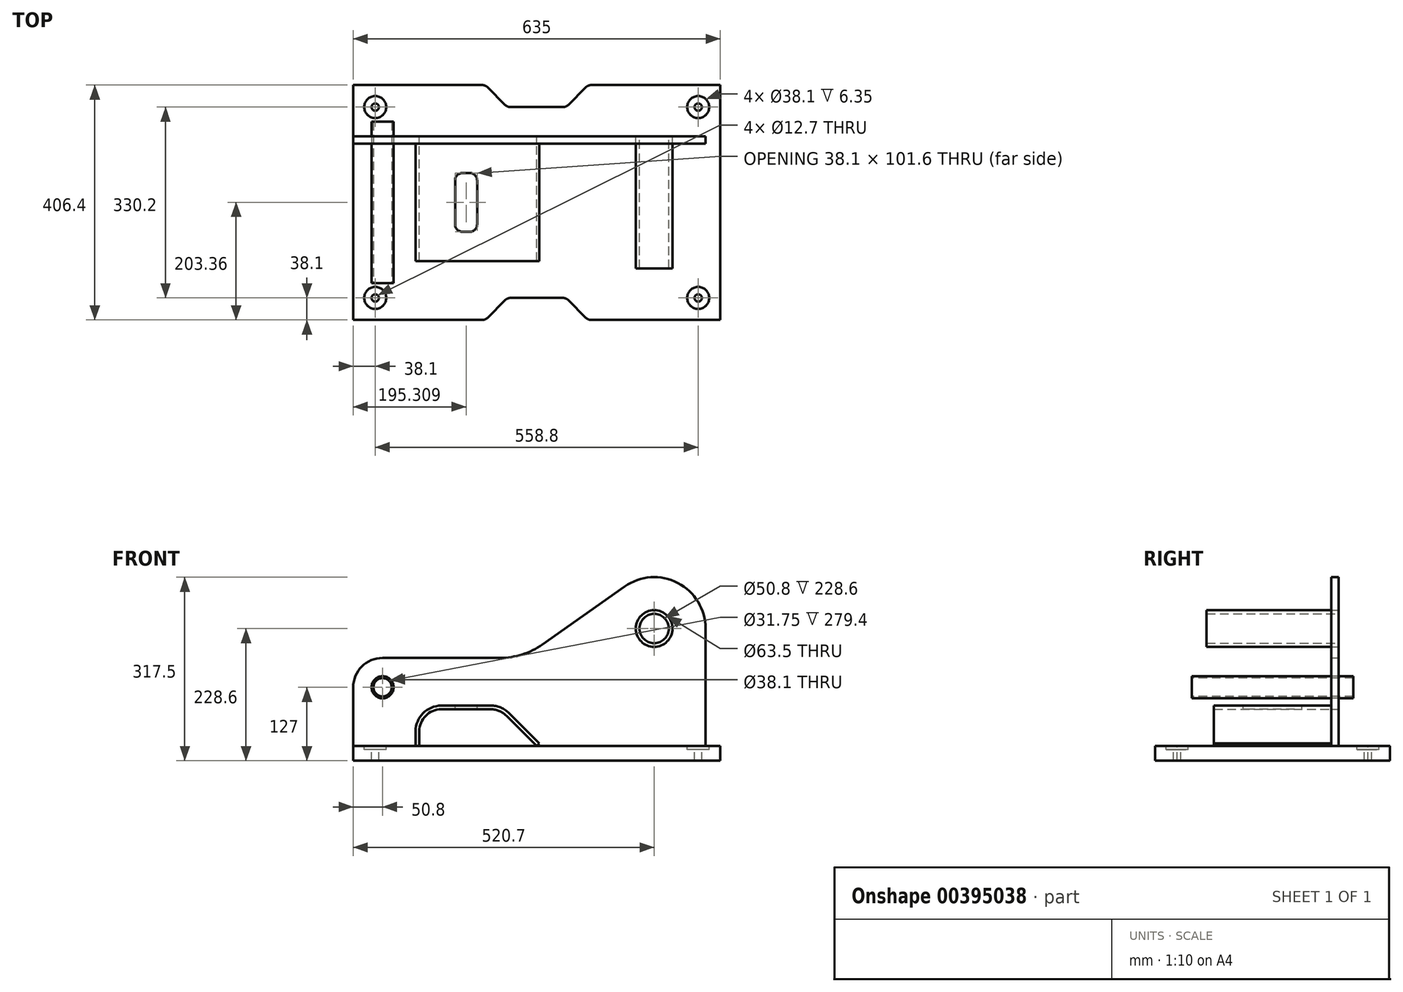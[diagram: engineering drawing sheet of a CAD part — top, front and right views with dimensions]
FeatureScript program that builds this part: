
annotation { "Feature Type Name" : "Feature", "Feature Type Description" : "" }
export const myFeature = defineFeature(function(context is Context, id is Id, definition is map)
    precondition{}
    {
        {
            var Q0;
            Q0=qCreatedBy(makeId("Front.planeOp"),FACE);
            var sketch = newSketch(context, id + "F0", { "sketchPlane" : qUnion([Q0])});
            skLineSegment(sketch, "E0.bottom", {"start": v(0, 0) * mm, "end": v(114.3, 0) * mm});
            skLineSegment(sketch, "E0.top", {"start": v(50.8, 152.4) * mm, "end": v(254, 152.4) * mm});
            skLineSegment(sketch, "E0.left", {"start": v(0, 0) * mm, "end": v(0, 101.6) * mm});
            skLineSegment(sketch, "E0.right", {"start": v(609.6, 0) * mm, "end": v(609.6, 203.2) * mm});
            skLineSegment(sketch, "E1", {"start": v(114.3, 0) * mm, "end": v(114.3, 25.4) * mm});
            skLineSegment(sketch, "E2", {"start": v(152.4, 63.5) * mm, "end": v(238.22, 63.5) * mm});
            skLineSegment(sketch, "E3", {"start": v(265.16, 52.34) * mm, "end": v(317.5, 0) * mm});
            skArc(sketch, "E4", {"start": v(609.6, 203.2) * mm, "mid": v(561.63, 282.11) * mm, "end": v(469.5, 275.87) * mm});
            skLineSegment(sketch, "E5", {"start": v(469.5, 275.87) * mm, "end": v(327.15, 175.58) * mm});
            skLineSegment(sketch, "E6.trimOffspring", {"start": v(317.5, 0) * mm, "end": v(609.6, 0) * mm});
            skPoint(sketch, "E7.visualSharp", {"position": v(294.25, 152.4) * mm});
            skArc(sketch, "E7.filletArc", {"start": v(254, 152.4) * mm, "mid": v(292.37, 158.33) * mm, "end": v(327.15, 175.58) * mm});
            skPoint(sketch, "E8.visualSharp", {"position": v(0, 152.4) * mm});
            skArc(sketch, "E8.filletArc", {"start": v(50.8, 152.4) * mm, "mid": v(14.88, 137.52) * mm, "end": v(0, 101.6) * mm});
            skPoint(sketch, "E9.visualSharp", {"position": v(114.3, 63.5) * mm});
            skArc(sketch, "E9.filletArc", {"start": v(152.4, 63.5) * mm, "mid": v(125.46, 52.34) * mm, "end": v(114.3, 25.4) * mm});
            skPoint(sketch, "E10.visualSharp", {"position": v(254, 63.5) * mm});
            skArc(sketch, "E10.filletArc", {"start": v(265.16, 52.34) * mm, "mid": v(252.8, 60.6) * mm, "end": v(238.22, 63.5) * mm});
            skPoint(sketch, "E11.visualSharp", {"position": v(317.5, 0) * mm});
            skCircle(sketch, "E12", {"center": v(520.7, 203.2) * mm, "radius": 31.75 * mm});
            skCircle(sketch, "E13", {"center": v(50.8, 101.6) * mm, "radius": 19.05 * mm});
            skPoint(sketch, "E14.orphan", {"position": v(342.9, 0) * mm});
            skSolve(sketch);
        }
        {
            var Q0;
            Q0 = qSketchRegion(id + "F0", true);
            extrude(context, id + "F1", {"entities" : qUnion([Q0]), "depth" : 12.7 * mm});
        }
        {
            var Q0;
            Q0=makeQuery(id+"F1.opExtrude","SWEPT_FACE",FACE,{"disambiguationData":[OSD([sQuery(id+"F0.wireOp",EDGE,"E6.trimOffspring")])]});
            var sketch = newSketch(context, id + "F2", { "sketchPlane" : qUnion([Q0])});
            skLineSegment(sketch, "E15.bottom", {"start": v(635, -88.74) * mm, "end": v(411.66, -88.74) * mm});
            skLineSegment(sketch, "E15.top", {"start": v(635, 317.66) * mm, "end": v(411.66, 317.66) * mm});
            skLineSegment(sketch, "E15.left", {"start": v(635, -88.74) * mm, "end": v(635, 317.66) * mm});
            skLineSegment(sketch, "E15.right", {"start": v(0, -88.74) * mm, "end": v(0, 317.66) * mm});
            skLineSegment(sketch, "E16", {"start": v(317.5, 317.66) * mm, "end": v(317.5, -88.74) * mm, "construction": true});
            skLineSegment(sketch, "E17", {"start": v(0, 114.46) * mm, "end": v(635, 114.46) * mm, "construction": true});
            skLineSegment(sketch, "E18", {"start": v(232.32, -85.02) * mm, "end": v(262.98, -54.36) * mm});
            skLineSegment(sketch, "E19", {"start": v(271.96, -50.64) * mm, "end": v(363.04, -50.64) * mm});
            skLineSegment(sketch, "E20", {"start": v(372.02, -54.36) * mm, "end": v(402.68, -85.02) * mm});
            skPoint(sketch, "E21", {"position": v(317.5, -50.64) * mm});
            skLineSegment(sketch, "E22.trimOffspring", {"start": v(223.34, -88.74) * mm, "end": v(0, -88.74) * mm});
            skPoint(sketch, "E23.visualSharp", {"position": v(266.7, -50.64) * mm});
            skArc(sketch, "E23.filletArc", {"start": v(271.96, -50.64) * mm, "mid": v(267.1, -51.6) * mm, "end": v(262.98, -54.36) * mm});
            skPoint(sketch, "E24.visualSharp", {"position": v(368.3, -50.64) * mm});
            skArc(sketch, "E24.filletArc", {"start": v(372.02, -54.36) * mm, "mid": v(367.9, -51.6) * mm, "end": v(363.04, -50.64) * mm});
            skPoint(sketch, "E25.visualSharp", {"position": v(406.4, -88.74) * mm});
            skArc(sketch, "E25.filletArc", {"start": v(402.68, -85.02) * mm, "mid": v(406.8, -87.77) * mm, "end": v(411.66, -88.74) * mm});
            skPoint(sketch, "E26.visualSharp", {"position": v(228.6, -88.74) * mm});
            skArc(sketch, "E26.filletArc", {"start": v(223.34, -88.74) * mm, "mid": v(228.2, -87.77) * mm, "end": v(232.32, -85.02) * mm});
            skLineSegment(sketch, "E27.MirrorCS", {"start": v(232.32, 313.94) * mm, "end": v(262.98, 283.28) * mm});
            skPoint(sketch, "E28.MirrorP", {"position": v(317.5, 279.56) * mm});
            skLineSegment(sketch, "E29.MirrorCS", {"start": v(271.96, 279.56) * mm, "end": v(363.04, 279.56) * mm});
            skLineSegment(sketch, "E30.MirrorCS", {"start": v(372.02, 283.28) * mm, "end": v(402.68, 313.94) * mm});
            skArc(sketch, "E31.MirrorCS", {"start": v(372.02, 283.28) * mm, "mid": v(367.9, 280.53) * mm, "end": v(363.04, 279.56) * mm});
            skArc(sketch, "E32.MirrorCS", {"start": v(271.96, 279.56) * mm, "mid": v(267.1, 280.53) * mm, "end": v(262.98, 283.28) * mm});
            skPoint(sketch, "E33.MirrorP", {"position": v(228.6, 317.66) * mm});
            skArc(sketch, "E34.MirrorCS", {"start": v(402.68, 313.94) * mm, "mid": v(406.8, 316.7) * mm, "end": v(411.66, 317.66) * mm});
            skArc(sketch, "E35.MirrorCS", {"start": v(223.34, 317.66) * mm, "mid": v(228.2, 316.7) * mm, "end": v(232.32, 313.94) * mm});
            skLineSegment(sketch, "E36.trimOffspring", {"start": v(223.34, 317.66) * mm, "end": v(0, 317.66) * mm});
            skSolve(sketch);
        }
        {
            var Q0;
            Q0 = qSketchRegion(id + "F2", true);
            extrude(context, id + "F3", {"entities" : qUnion([Q0]), "depth" : 25.4 * mm});
        }
        {
            var Q0;
            Q0=makeQuery(id+"F1.opExtrude","CAP_FACE",FACE,{"disambiguationData":[OSD([sQuery(id+"F0.wireOp",EDGE,"E0.bottom"),sQuery(id+"F0.wireOp",EDGE,"E0.top"),sQuery(id+"F0.wireOp",EDGE,"E0.left"),sQuery(id+"F0.wireOp",EDGE,"E0.right"),sQuery(id+"F0.wireOp",EDGE,"E1"),sQuery(id+"F0.wireOp",EDGE,"E2"),sQuery(id+"F0.wireOp",EDGE,"E3"),sQuery(id+"F0.wireOp",EDGE,"E4"),sQuery(id+"F0.wireOp",EDGE,"E5"),sQuery(id+"F0.wireOp",EDGE,"E6.trimOffspring"),sQuery(id+"F0.wireOp",EDGE,"E7.filletArc"),sQuery(id+"F0.wireOp",EDGE,"E8.filletArc"),sQuery(id+"F0.wireOp",EDGE,"E9.filletArc"),sQuery(id+"F0.wireOp",EDGE,"E10.filletArc"),sQuery(id+"F0.wireOp",EDGE,"E12"),sQuery(id+"F0.wireOp",EDGE,"E13")])],"isStart":false});
            var sketch = newSketch(context, id + "F4", { "sketchPlane" : qUnion([Q0])});
            skLineSegment(sketch, "E37.0", {"start": v(114.3, 0) * mm, "end": v(114.3, 25.4) * mm});
            skArc(sketch, "E38.0", {"start": v(152.4, 63.5) * mm, "mid": v(125.46, 52.34) * mm, "end": v(114.3, 25.4) * mm});
            skLineSegment(sketch, "E39.0", {"start": v(152.4, 63.5) * mm, "end": v(238.22, 63.5) * mm});
            skArc(sketch, "E40.0", {"start": v(265.16, 52.34) * mm, "mid": v(252.8, 60.6) * mm, "end": v(238.22, 63.5) * mm});
            skLineSegment(sketch, "E41.0", {"start": v(265.16, 52.34) * mm, "end": v(317.5, 0) * mm});
            skLineSegment(sketch, "E42.0", {"start": v(269.65, 56.83) * mm, "end": v(322, 4.5) * mm});
            skLineSegment(sketch, "E42.1", {"start": v(107.95, 0) * mm, "end": v(107.95, 25.4) * mm});
            skArc(sketch, "E42.2", {"start": v(152.4, 69.85) * mm, "mid": v(120.97, 56.83) * mm, "end": v(107.95, 25.4) * mm});
            skLineSegment(sketch, "E42.3", {"start": v(152.4, 69.85) * mm, "end": v(238.22, 69.85) * mm});
            skArc(sketch, "E42.4", {"start": v(269.65, 56.83) * mm, "mid": v(255.23, 66.47) * mm, "end": v(238.22, 69.85) * mm});
            skLineSegment(sketch, "E43", {"start": v(322, 4.5) * mm, "end": v(317.5, 0) * mm});
            skLineSegment(sketch, "E44", {"start": v(107.95, 0) * mm, "end": v(114.3, 0) * mm});
            skSolve(sketch);
        }
        {
            var Q0;
            Q0 = qSketchRegion(id + "F4", true);
            extrude(context, id + "F5", {"entities" : qUnion([Q0]), "depth" : 203.2 * mm});
        }
        {
            var Q0;
            Q0=makeQuery(id+"F1.opExtrude","CAP_FACE",FACE,{"disambiguationData":[OSD([sQuery(id+"F0.wireOp",EDGE,"E0.bottom"),sQuery(id+"F0.wireOp",EDGE,"E0.top"),sQuery(id+"F0.wireOp",EDGE,"E0.left"),sQuery(id+"F0.wireOp",EDGE,"E0.right"),sQuery(id+"F0.wireOp",EDGE,"E1"),sQuery(id+"F0.wireOp",EDGE,"E2"),sQuery(id+"F0.wireOp",EDGE,"E3"),sQuery(id+"F0.wireOp",EDGE,"E4"),sQuery(id+"F0.wireOp",EDGE,"E5"),sQuery(id+"F0.wireOp",EDGE,"E6.trimOffspring"),sQuery(id+"F0.wireOp",EDGE,"E7.filletArc"),sQuery(id+"F0.wireOp",EDGE,"E8.filletArc"),sQuery(id+"F0.wireOp",EDGE,"E9.filletArc"),sQuery(id+"F0.wireOp",EDGE,"E10.filletArc"),sQuery(id+"F0.wireOp",EDGE,"E12"),sQuery(id+"F0.wireOp",EDGE,"E13")])],"isStart":true});
            var sketch = newSketch(context, id + "F6", { "sketchPlane" : qUnion([Q0])});
            skCircle(sketch, "E45.0", {"center": v(-520.7, 203.2) * mm, "radius": 31.75 * mm});
            skCircle(sketch, "E46.0", {"center": v(-520.7, 203.2) * mm, "radius": 25.4 * mm});
            skSolve(sketch);
        }
        {
            var Q0;
            Q0 = qSketchRegion(id + "F6", true);
            extrude(context, id + "F7", {"entities" : qUnion([Q0]), "oppositeDirection" : true, "depth" : 228.6 * mm});
        }
        {
            var Q0;
            Q0=makeQuery(id+"F3.opExtrude","CAP_FACE",FACE,{"disambiguationData":[OSD([sQuery(id+"F2.wireOp",EDGE,"E15.bottom"),sQuery(id+"F2.wireOp",EDGE,"E15.top"),sQuery(id+"F2.wireOp",EDGE,"E15.left"),sQuery(id+"F2.wireOp",EDGE,"E15.right"),sQuery(id+"F2.wireOp",EDGE,"E18"),sQuery(id+"F2.wireOp",EDGE,"E19"),sQuery(id+"F2.wireOp",EDGE,"E20"),sQuery(id+"F2.wireOp",EDGE,"E22.trimOffspring"),sQuery(id+"F2.wireOp",EDGE,"E23.filletArc"),sQuery(id+"F2.wireOp",EDGE,"E24.filletArc"),sQuery(id+"F2.wireOp",EDGE,"E25.filletArc"),sQuery(id+"F2.wireOp",EDGE,"E26.filletArc"),sQuery(id+"F2.wireOp",EDGE,"E27.MirrorCS"),sQuery(id+"F2.wireOp",EDGE,"E29.MirrorCS"),sQuery(id+"F2.wireOp",EDGE,"E30.MirrorCS"),sQuery(id+"F2.wireOp",EDGE,"E31.MirrorCS"),sQuery(id+"F2.wireOp",EDGE,"E32.MirrorCS"),sQuery(id+"F2.wireOp",EDGE,"E34.MirrorCS"),sQuery(id+"F2.wireOp",EDGE,"E35.MirrorCS"),sQuery(id+"F2.wireOp",EDGE,"E36.trimOffspring")])],"isStart":true});
            var sketch = newSketch(context, id + "F8", { "sketchPlane" : qUnion([Q0])});
            skCircle(sketch, "E47", {"center": v(596.9, 50.64) * mm, "radius": 19.05 * mm});
            skCircle(sketch, "E48", {"center": v(596.9, 50.64) * mm, "radius": 6.35 * mm});
            skCircle(sketch, "E49.MirrorC", {"center": v(38.1, 50.64) * mm, "radius": 19.05 * mm});
            skCircle(sketch, "E50.MirrorC", {"center": v(38.1, 50.64) * mm, "radius": 6.35 * mm});
            skCircle(sketch, "E51.MirrorC", {"center": v(38.1, -279.56) * mm, "radius": 19.05 * mm});
            skCircle(sketch, "E52.MirrorC", {"center": v(38.1, -279.56) * mm, "radius": 6.35 * mm});
            skCircle(sketch, "E53.MirrorC", {"center": v(596.9, -279.56) * mm, "radius": 19.05 * mm});
            skCircle(sketch, "E54.MirrorC", {"center": v(596.9, -279.56) * mm, "radius": 6.35 * mm});
            skSolve(sketch);
        }
        {
            var Q0;
            Q0 = qSketchRegion(id + "F8", true);
            var Q1;
            Q1=makeQuery(id+"F8.imprint","IMPRINT",FACE,{"disambiguationData":[TD([[makeQuery(id+"F8.imprint","IMPRINT",EDGE,{"derivedFrom":sQuery(id+"F8.wireOp",EDGE,"E54.MirrorC")}),-1.0]])]});
            var Q2;
            Q2=makeQuery(id+"F8.imprint","IMPRINT",FACE,{"disambiguationData":[TD([[makeQuery(id+"F8.imprint","IMPRINT",EDGE,{"derivedFrom":sQuery(id+"F8.wireOp",EDGE,"E48")}),1.0]])]});
            var Q3;
            Q3=makeQuery(id+"F8.imprint","IMPRINT",FACE,{"disambiguationData":[TD([[makeQuery(id+"F8.imprint","IMPRINT",EDGE,{"derivedFrom":sQuery(id+"F8.wireOp",EDGE,"E52.MirrorC")}),1.0]])]});
            var Q4;
            Q4=makeQuery(id+"F8.imprint","IMPRINT",FACE,{"disambiguationData":[TD([[makeQuery(id+"F8.imprint","IMPRINT",EDGE,{"derivedFrom":sQuery(id+"F8.wireOp",EDGE,"E50.MirrorC")}),-1.0]])]});
            extrude(context, id + "F9", {"entities" : qUnion([Q0, Q1, Q2, Q3, Q4]), "operationType" : NewBodyOperationType.REMOVE, "oppositeDirection" : true, "depth" : 12.7 * mm, "symmetric" : true});
        }
        {
            var Q0;
            Q0=sQuery(id+"F8.wireOp",VERTEX,"E52.MirrorC.center");
            var Q1;
            Q1=sQuery(id+"F8.wireOp",VERTEX,"E50.MirrorC.center");
            var Q2;
            Q2=sQuery(id+"F8.wireOp",VERTEX,"E54.MirrorC.center");
            var Q3;
            Q3=sQuery(id+"F8.wireOp",VERTEX,"E48.center");
            var Q4;
            Q4=makeQuery(id+"F3.opExtrude","SWEPT_BODY",BODY,{"disambiguationData":[OSD([sQuery(id+"F2.wireOp",EDGE,"E15.bottom"),sQuery(id+"F2.wireOp",EDGE,"E15.top"),sQuery(id+"F2.wireOp",EDGE,"E15.left"),sQuery(id+"F2.wireOp",EDGE,"E15.right"),sQuery(id+"F2.wireOp",EDGE,"E18"),sQuery(id+"F2.wireOp",EDGE,"E19"),sQuery(id+"F2.wireOp",EDGE,"E20"),sQuery(id+"F2.wireOp",EDGE,"E22.trimOffspring"),sQuery(id+"F2.wireOp",EDGE,"E23.filletArc"),sQuery(id+"F2.wireOp",EDGE,"E24.filletArc"),sQuery(id+"F2.wireOp",EDGE,"E25.filletArc"),sQuery(id+"F2.wireOp",EDGE,"E26.filletArc"),sQuery(id+"F2.wireOp",EDGE,"E27.MirrorCS"),sQuery(id+"F2.wireOp",EDGE,"E29.MirrorCS"),sQuery(id+"F2.wireOp",EDGE,"E30.MirrorCS"),sQuery(id+"F2.wireOp",EDGE,"E31.MirrorCS"),sQuery(id+"F2.wireOp",EDGE,"E32.MirrorCS"),sQuery(id+"F2.wireOp",EDGE,"E34.MirrorCS"),sQuery(id+"F2.wireOp",EDGE,"E35.MirrorCS"),sQuery(id+"F2.wireOp",EDGE,"E36.trimOffspring")])]});
            hole(context, id + "F10", {"style" : HoleStyle.SIMPLE, "endStyle" : HoleEndStyle.THROUGH, "holeDiameter" : 12.7 * mm, "isTappedThrough" : true, "tappedDepth" : 12.7 * mm, "tapClearance" : 3, "locations" : qUnion([Q0, Q1, Q2, Q3]), "scope" : qUnion([Q4])});
        }
        {
            var Q0;
            Q0=makeQuery(id+"F1.opExtrude","CAP_FACE",FACE,{"disambiguationData":[OSD([sQuery(id+"F0.wireOp",EDGE,"E0.bottom"),sQuery(id+"F0.wireOp",EDGE,"E0.top"),sQuery(id+"F0.wireOp",EDGE,"E0.left"),sQuery(id+"F0.wireOp",EDGE,"E0.right"),sQuery(id+"F0.wireOp",EDGE,"E1"),sQuery(id+"F0.wireOp",EDGE,"E2"),sQuery(id+"F0.wireOp",EDGE,"E3"),sQuery(id+"F0.wireOp",EDGE,"E4"),sQuery(id+"F0.wireOp",EDGE,"E5"),sQuery(id+"F0.wireOp",EDGE,"E6.trimOffspring"),sQuery(id+"F0.wireOp",EDGE,"E7.filletArc"),sQuery(id+"F0.wireOp",EDGE,"E8.filletArc"),sQuery(id+"F0.wireOp",EDGE,"E9.filletArc"),sQuery(id+"F0.wireOp",EDGE,"E10.filletArc"),sQuery(id+"F0.wireOp",EDGE,"E12"),sQuery(id+"F0.wireOp",EDGE,"E13")])],"isStart":true});
            var sketch = newSketch(context, id + "F11", { "sketchPlane" : qUnion([Q0])});
            skCircle(sketch, "E55.0", {"center": v(-50.8, 101.6) * mm, "radius": 19.05 * mm});
            skCircle(sketch, "E56.0", {"center": v(-50.8, 101.6) * mm, "radius": 15.88 * mm});
            skSolve(sketch);
        }
        {
            var Q0;
            Q0 = qSketchRegion(id + "F11", true);
            extrude(context, id + "F12", {"entities" : qUnion([Q0]), "depth" : 25.4 * mm, "hasSecondDirection" : true, "secondDirectionOppositeDirection" : true, "secondDirectionDepth" : 254 * mm});
        }
        {
            var Q0;
            Q0=makeQuery(id+"F5.opExtrude","SWEPT_FACE",FACE,{"disambiguationData":[OSD([sQuery(id+"F4.wireOp",EDGE,"E42.3")])]});
            var sketch = newSketch(context, id + "F13", { "sketchPlane" : qUnion([Q0])});
            skLineSegment(sketch, "E57.bottom", {"start": v(188.96, -63.5) * mm, "end": v(201.66, -63.5) * mm});
            skLineSegment(sketch, "E57.top", {"start": v(188.96, -165.1) * mm, "end": v(201.66, -165.1) * mm});
            skLineSegment(sketch, "E57.left", {"start": v(176.26, -76.2) * mm, "end": v(176.26, -152.4) * mm});
            skLineSegment(sketch, "E57.right", {"start": v(214.36, -76.2) * mm, "end": v(214.36, -152.4) * mm});
            skPoint(sketch, "E57.middle", {"position": v(195.3, -114.3) * mm});
            skPoint(sketch, "E58.visualSharp", {"position": v(176.26, -63.5) * mm});
            skArc(sketch, "E58.filletArc", {"start": v(188.96, -63.5) * mm, "mid": v(179.98, -67.22) * mm, "end": v(176.26, -76.2) * mm});
            skPoint(sketch, "E59.visualSharp", {"position": v(214.36, -63.5) * mm});
            skArc(sketch, "E59.filletArc", {"start": v(214.36, -76.2) * mm, "mid": v(210.64, -67.22) * mm, "end": v(201.66, -63.5) * mm});
            skPoint(sketch, "E60.visualSharp", {"position": v(214.36, -165.1) * mm});
            skArc(sketch, "E60.filletArc", {"start": v(201.66, -165.1) * mm, "mid": v(210.64, -161.38) * mm, "end": v(214.36, -152.4) * mm});
            skPoint(sketch, "E61.visualSharp", {"position": v(176.26, -165.1) * mm});
            skArc(sketch, "E61.filletArc", {"start": v(176.26, -152.4) * mm, "mid": v(179.98, -161.38) * mm, "end": v(188.96, -165.1) * mm});
            skSolve(sketch);
        }
        {
            var Q0;
            Q0 = qSketchRegion(id + "F13", true);
            extrude(context, id + "F14", {"entities" : qUnion([Q0]), "operationType" : NewBodyOperationType.REMOVE, "oppositeDirection" : true, "depth" : 25.4 * mm});
        }
    });
